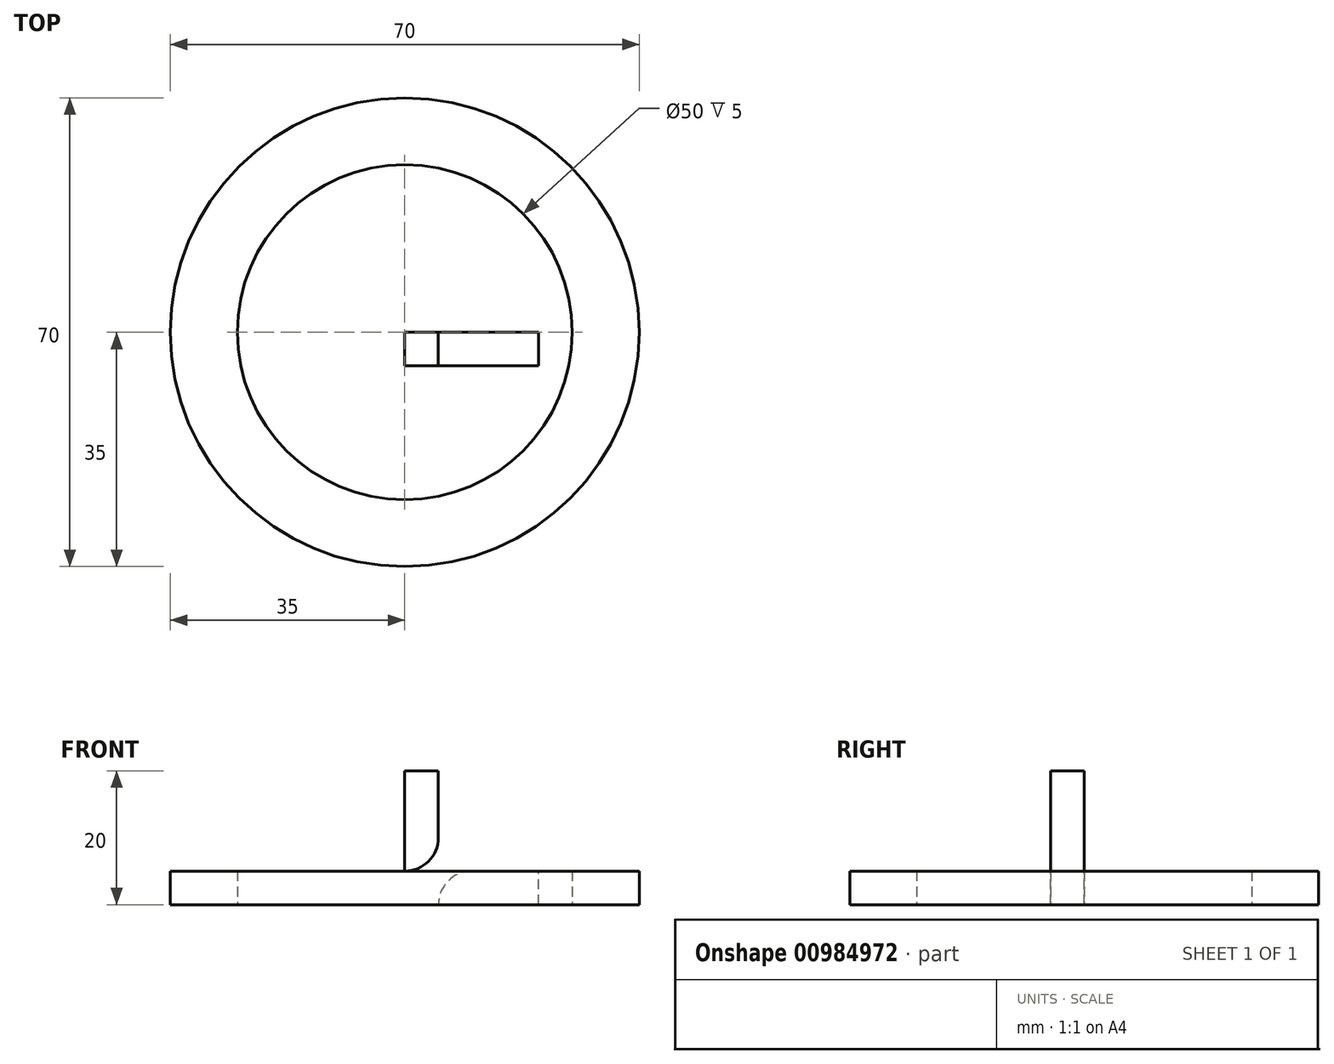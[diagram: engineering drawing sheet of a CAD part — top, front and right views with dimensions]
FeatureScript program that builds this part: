
annotation { "Feature Type Name" : "Feature", "Feature Type Description" : "" }
export const myFeature = defineFeature(function(context is Context, id is Id, definition is map)
    precondition{}
    {
        {
            var Q0;
            Q0=qCreatedBy(makeId("Top.planeOp"),FACE);
            var sketch = newSketch(context, id + "F0", { "sketchPlane" : qUnion([Q0])});
            skCircle(sketch, "E0", {"center": v(0, 0) * mm, "radius": 25 * mm});
            skCircle(sketch, "E1", {"center": v(0, 0) * mm, "radius": 35 * mm});
            skSolve(sketch);
        }
        {
            var Q0;
            Q0=makeQuery(id+"F0.imprint","IMPRINT",FACE,{"disambiguationData":[TD([[makeQuery(id+"F0.imprint","IMPRINT",EDGE,{"derivedFrom":sQuery(id+"F0.wireOp",EDGE,"E0")}),-1.0]])]});
            extrude(context, id + "F1", {"entities" : qUnion([Q0]), "depth" : 5 * mm, "offsetDistance" : 25 * mm});
        }
        {
            assignVariable(context, id + "F2", {"name" : "thk", "anyValue" : 5});
        }
        {
            var Q0;
            Q0=qCreatedBy(makeId("Front.planeOp"),FACE);
            var sketch = newSketch(context, id + "F3", { "sketchPlane" : qUnion([Q0])});
            skLineSegment(sketch, "E2.bottom", {"start": v(0, 0) * mm, "end": v(5, 0) * mm});
            skLineSegment(sketch, "E2.top", {"start": v(0, 20) * mm, "end": v(5, 20) * mm});
            skLineSegment(sketch, "E2.left", {"start": v(0, 0) * mm, "end": v(0, 20) * mm});
            skLineSegment(sketch, "E2.right", {"start": v(5, 0) * mm, "end": v(5, 20) * mm});
            skLineSegment(sketch, "E3.bottom", {"start": v(0, 0) * mm, "end": v(20, 0) * mm});
            skLineSegment(sketch, "E3.top", {"start": v(0, 5) * mm, "end": v(20, 5) * mm});
            skLineSegment(sketch, "E3.left", {"start": v(0, 0) * mm, "end": v(0, 5) * mm});
            skLineSegment(sketch, "E3.right", {"start": v(20, 0) * mm, "end": v(20, 5) * mm});
            skSolve(sketch);
        }
        {
            var Q0;
            {var subQ5=sQuery(id+"F3.wireOp",EDGE,"E3.right");Q0=makeQuery(id+"F3.imprint","IMPRINT",FACE,{"disambiguationData":[TD([[makeQuery(id+"F3.imprint","IMPRINT",EDGE,{"derivedFrom":subQ5}),1.0]])]});}
            var Q1;
            {var subQ5=sQuery(id+"F3.wireOp",EDGE,"E3.left");Q1=makeQuery(id+"F3.imprint","IMPRINT",FACE,{"disambiguationData":[TD([[makeQuery(id+"F3.imprint","IMPRINT",EDGE,{"derivedFrom":subQ5}),-1.0]])]});}
            var Q2;
            {var subQ0=sQuery(id+"F3.wireOp",EDGE,"E2.top");Q2=makeQuery(id+"F3.imprint","IMPRINT",FACE,{"disambiguationData":[TD([[makeQuery(id+"F3.imprint","IMPRINT",EDGE,{"derivedFrom":subQ0}),-1.0]])]});}
            extrude(context, id + "F4", {"entities" : qUnion([Q0, Q1, Q2]), "depth" : (getVariable(context, 'thk')) * mm, "offsetDistance" : 25 * mm});
        }
        {
            var Q0;
            Q0=makeQuery(id+"F4.opExtrude","SWEPT_EDGE",EDGE,{"disambiguationData":[OSD([sQuery(id+"F3.wireOp",EDGE,"E2.right"),sQuery(id+"F3.wireOp",EDGE,"E3.top")])]});
            fillet(context, id + "F5", {"entities" : qUnion([Q0]), "radius" : 5 * mm, "tangentPropagation" : true, "allowEdgeOverflow" : false});
        }
    });
